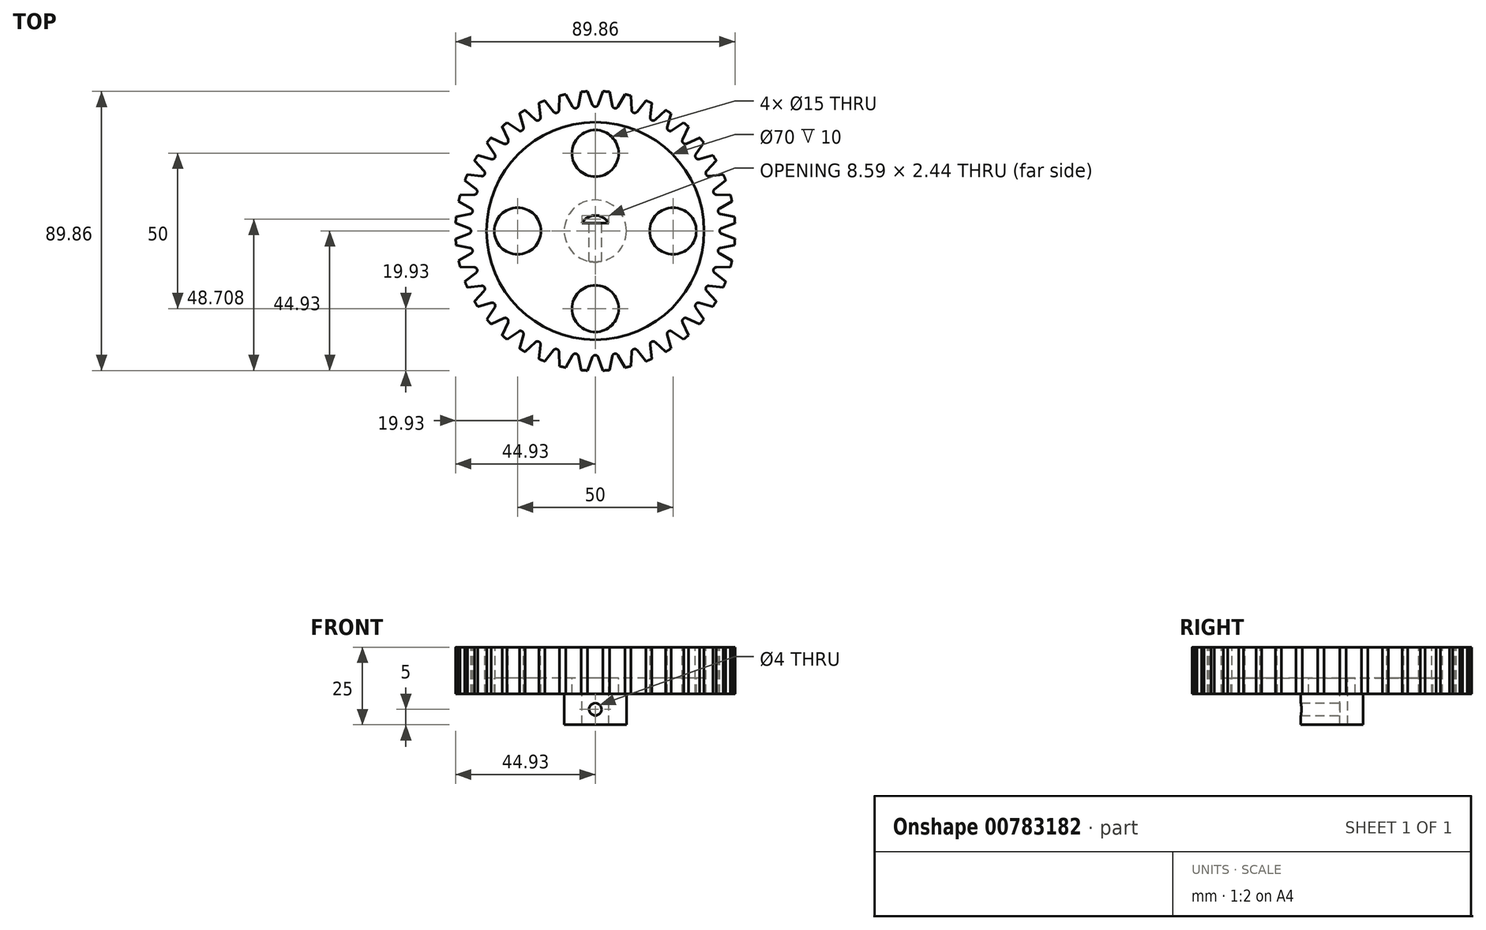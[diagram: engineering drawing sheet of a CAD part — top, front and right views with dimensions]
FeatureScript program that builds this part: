
annotation { "Feature Type Name" : "Feature", "Feature Type Description" : "" }
export const myFeature = defineFeature(function(context is Context, id is Id, definition is map)
    precondition{}
    {
        {
            var Q0;
            Q0=qCreatedBy(makeId("Top.planeOp"),FACE);
            var sketch = newSketch(context, id + "F0", { "sketchPlane" : qUnion([Q0])});
            skCircle(sketch, "E0", {"center": v(0, 0) * mm, "radius": 45 * mm});
            skCircle(sketch, "E1", {"center": v(0, 0) * mm, "radius": 5 * mm});
            skCircle(sketch, "E2", {"center": v(0, 0) * mm, "radius": 25 * mm});
            skCircle(sketch, "E3", {"center": v(0, 25) * mm, "radius": 7.5 * mm});
            skCircle(sketch, "E4", {"center": v(0, 0) * mm, "radius": 35 * mm});
            skLineSegment(sketch, "E5", {"start": v(4.31, 2.56) * mm, "end": v(-4.3, 2.56) * mm});
            skCircle(sketch, "E6", {"center": v(0, 0) * mm, "radius": 10 * mm});
            skCircle(sketch, "E7.1.0", {"center": v(-25, 0) * mm, "radius": 7.5 * mm});
            skCircle(sketch, "E7.2.0", {"center": v(0, -25) * mm, "radius": 7.5 * mm});
            skCircle(sketch, "E7.3.0", {"center": v(25, 0) * mm, "radius": 7.5 * mm});
            skCircle(sketch, "E8", {"center": v(0, 0) * mm, "radius": 40 * mm});
            skSolve(sketch);
        }
        {
            var Q0;
            Q0=makeQuery(id+"F0.imprint","IMPRINT",FACE,{"disambiguationData":[TD([[makeQuery(id+"F0.imprint","IMPRINT",EDGE,{"derivedFrom":sQuery(id+"F0.wireOp",EDGE,"E4")}),1.0]])]});
            var Q1;
            Q1=makeQuery(id+"F0.imprint","IMPRINT",FACE,{"disambiguationData":[TD([[makeQuery(id+"F0.imprint","IMPRINT",EDGE,{"derivedFrom":sQuery(id+"F0.wireOp",EDGE,"E6")}),-1.0]])]});
            extrude(context, id + "F1", {"entities" : qUnion([Q0, Q1]), "oppositeDirection" : true, "depth" : 5 * mm, "offsetDistance" : 25 * mm});
        }
        {
            var Q0;
            Q0=makeQuery(id+"F0.imprint","IMPRINT",FACE,{"disambiguationData":[TD([[makeQuery(id+"F0.imprint","IMPRINT",EDGE,{"derivedFrom":sQuery(id+"F0.wireOp",EDGE,"E6")}),1.0]])]});
            var Q1;
            {var subQ0=sQuery(id+"F0.wireOp",EDGE,"E5");var subQ1=sQuery(id+"F0.wireOp",EDGE,"E1");var subQ2=makeQuery(id+"F0.imprint","INTERSECT",VERTEX,{"disambiguationData":[OD(0.0)],"derivedFrom":[subQ1,subQ0]});Q1=makeQuery(id+"F0.imprint","IMPRINT",FACE,{"disambiguationData":[TD([[makeQuery(id+"F0.imprint","IMPRINT",EDGE,{"disambiguationData":[TD([[subQ2,1.0]])],"derivedFrom":subQ1}),1.0]])]});}
            extrude(context, id + "F2", {"entities" : qUnion([Q0, Q1]), "operationType" : NewBodyOperationType.ADD, "oppositeDirection" : true, "depth" : 15 * mm, "offsetDistance" : 25 * mm});
        }
        {
            var Q0;
            Q0=makeQuery(id+"F2.opExtrude","SWEPT_FACE",FACE,{"disambiguationData":[OSD([sQuery(id+"F0.wireOp",EDGE,"E5")])]});
            var sketch = newSketch(context, id + "F3", { "sketchPlane" : qUnion([Q0])});
            skCircle(sketch, "E9", {"center": v(0, -10) * mm, "radius": 2 * mm});
            skSolve(sketch);
        }
        {
            var Q0;
            Q0 = qSketchRegion(id + "F3", true);
            extrude(context, id + "F4", {"entities" : qUnion([Q0]), "operationType" : NewBodyOperationType.REMOVE, "endBound" : BoundingType.THROUGH_ALL, "oppositeDirection" : true, "depth" : 25 * mm, "offsetDistance" : 25 * mm});
        }
        {
            var Q0;
            Q0=makeQuery(id+"F0.imprint","IMPRINT",FACE,{"disambiguationData":[TD([[makeQuery(id+"F0.imprint","IMPRINT",EDGE,{"derivedFrom":sQuery(id+"F0.wireOp",EDGE,"E4")}),-1.0]])]});
            var Q1;
            Q1=makeQuery(id+"F0.imprint","IMPRINT",FACE,{"disambiguationData":[TD([[makeQuery(id+"F0.imprint","IMPRINT",EDGE,{"derivedFrom":sQuery(id+"F0.wireOp",EDGE,"E0")}),1.0]])]});
            extrude(context, id + "F5", {"entities" : qUnion([Q0, Q1]), "operationType" : NewBodyOperationType.ADD, "oppositeDirection" : true, "depth" : 5 * mm, "offsetDistance" : 25 * mm});
        }
        {
            var Q0;
            Q0=makeQuery(id+"F0.imprint","IMPRINT",FACE,{"disambiguationData":[TD([[makeQuery(id+"F0.imprint","IMPRINT",EDGE,{"derivedFrom":sQuery(id+"F0.wireOp",EDGE,"E0")}),1.0]])]});
            var Q1;
            Q1=makeQuery(id+"F0.imprint","IMPRINT",FACE,{"disambiguationData":[TD([[makeQuery(id+"F0.imprint","IMPRINT",EDGE,{"derivedFrom":sQuery(id+"F0.wireOp",EDGE,"E4")}),-1.0]])]});
            extrude(context, id + "F6", {"entities" : qUnion([Q0, Q1]), "operationType" : NewBodyOperationType.ADD, "depth" : 10 * mm, "offsetDistance" : 25 * mm});
        }
        {
            var Q0;
            Q0=makeQuery(id+"F6.opExtrude","CAP_FACE",FACE,{"disambiguationData":[OSD([sQuery(id+"F0.wireOp",EDGE,"E0"),sQuery(id+"F0.wireOp",EDGE,"E4")])],"isStart":false});
            var sketch = newSketch(context, id + "F7", { "sketchPlane" : qUnion([Q0])});
            skPoint(sketch, "E10.orphan", {"position": v(0, 0) * mm});
            skLineSegment(sketch, "E11", {"start": v(2.5, 44.93) * mm, "end": v(0.94, 40.66) * mm});
            skLineSegment(sketch, "E12", {"start": v(0, 40) * mm, "end": v(0, 40) * mm});
            skPoint(sketch, "E13.visualSharp", {"position": v(0.7, 40) * mm});
            skArc(sketch, "E13.filletArc", {"start": v(0, 40) * mm, "mid": v(0.57, 40.18) * mm, "end": v(0.94, 40.66) * mm});
            skLineSegment(sketch, "E14.MirrorCS", {"start": v(-2.5, 44.93) * mm, "end": v(-0.94, 40.66) * mm});
            skArc(sketch, "E15.MirrorCS", {"start": v(0, 40) * mm, "mid": v(-0.57, 40.18) * mm, "end": v(-0.94, 40.66) * mm});
            skSolve(sketch);
        }
        {
            var Q0;
            {var subQ1=sQuery(id+"F7.wireOp",EDGE,"E11");Q0=makeQuery(id+"F7.imprint","IMPRINT",FACE,{"disambiguationData":[TD([[makeQuery(id+"F7.imprint","IMPRINT",EDGE,{"derivedFrom":subQ1}),-1.0]])]});}
            extrude(context, id + "F8", {"entities" : qUnion([Q0]), "operationType" : NewBodyOperationType.REMOVE, "endBound" : BoundingType.THROUGH_ALL, "oppositeDirection" : true, "depth" : 25 * mm, "offsetDistance" : 25 * mm});
        }
        {
            var Q0;
            Q0=makeQuery(id+"F8.boolean.opBoolean","COPY",FACE,{"derivedFrom":makeQuery(id+"F8.opExtrude","SWEPT_FACE",FACE,{"disambiguationData":[OSD([sQuery(id+"F7.wireOp",EDGE,"E14.MirrorCS")])]})});
            var Q1;
            Q1=makeQuery(id+"F8.boolean.opBoolean","COPY",FACE,{"derivedFrom":makeQuery(id+"F8.opExtrude","SWEPT_FACE",FACE,{"disambiguationData":[OSD([sQuery(id+"F7.wireOp",EDGE,"E15.MirrorCS")])]})});
            var Q2;
            Q2=makeQuery(id+"F8.boolean.opBoolean","COPY",FACE,{"derivedFrom":makeQuery(id+"F8.opExtrude","SWEPT_FACE",FACE,{"disambiguationData":[OSD([sQuery(id+"F7.wireOp",EDGE,"E12"),sQuery(id+"F7.wireOp",EDGE,"E12")])]})});
            var Q3;
            Q3=makeQuery(id+"F8.boolean.opBoolean","COPY",FACE,{"derivedFrom":makeQuery(id+"F8.opExtrude","SWEPT_FACE",FACE,{"disambiguationData":[OSD([sQuery(id+"F7.wireOp",EDGE,"E13.filletArc")])]})});
            var Q4;
            Q4=makeQuery(id+"F8.boolean.opBoolean","COPY",FACE,{"derivedFrom":makeQuery(id+"F8.opExtrude","SWEPT_FACE",FACE,{"disambiguationData":[OSD([sQuery(id+"F7.wireOp",EDGE,"E11")])]})});
            var Q5;
            Q5=makeQuery(id+"F2.opExtrude","SWEPT_FACE",FACE,{"disambiguationData":[OSD([sQuery(id+"F0.wireOp",EDGE,"E1")])]});
            circularPattern(context, id + "F9", {"patternType" : PatternType.FACE, "operationType" : NewBodyOperationType.REMOVE, "faces" : qUnion([Q0, Q1, Q2, Q3, Q4]), "axis" : qUnion([Q5]), "angle" : 9 * degree, "instanceCount" : 40});
        }
    });
